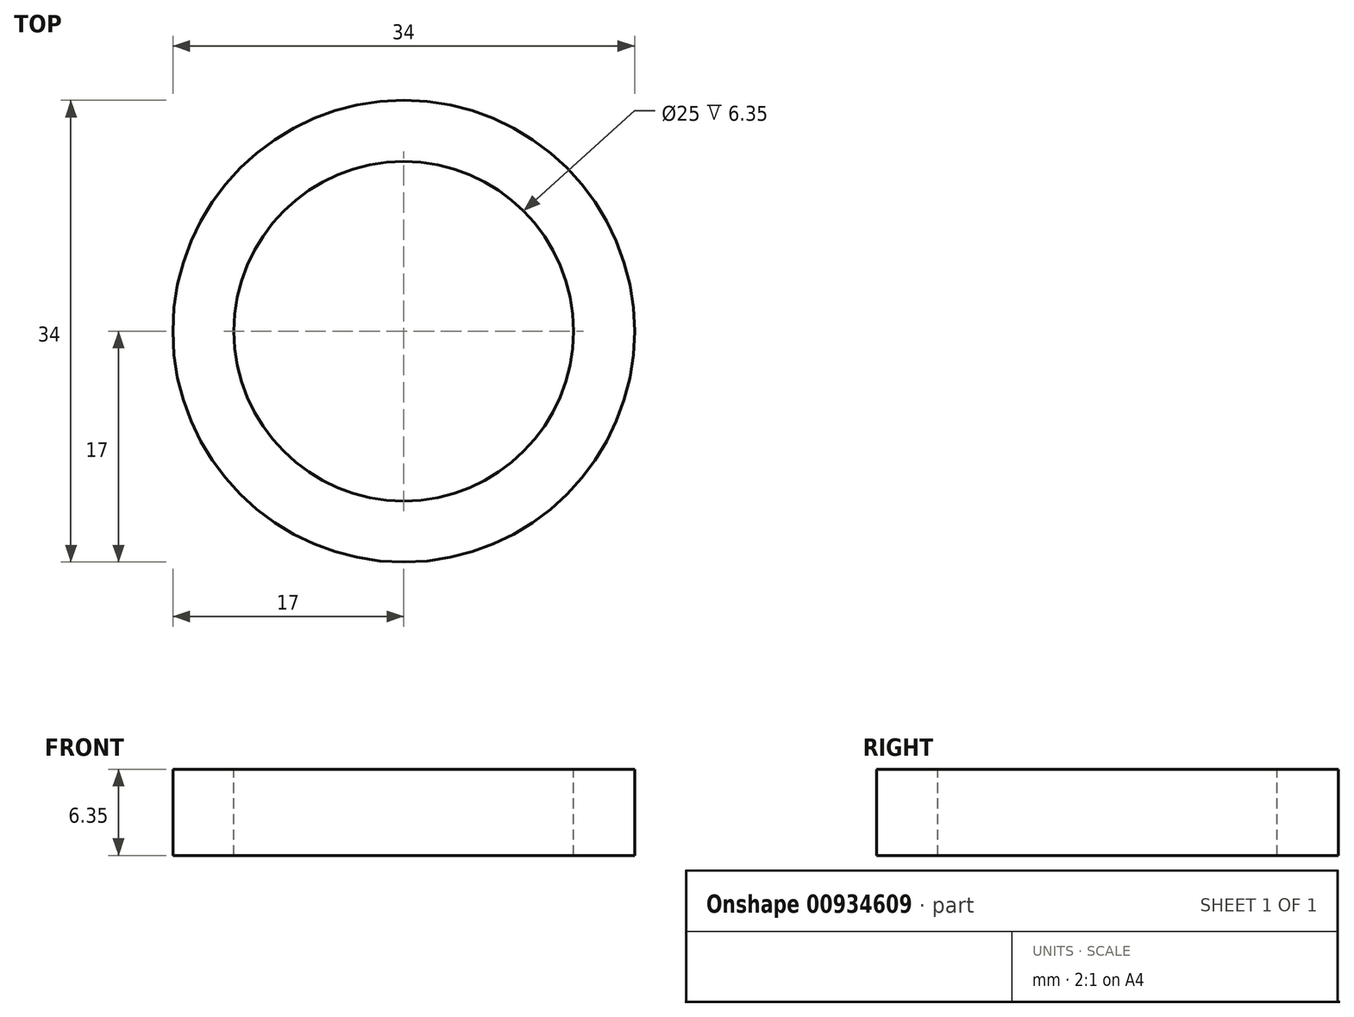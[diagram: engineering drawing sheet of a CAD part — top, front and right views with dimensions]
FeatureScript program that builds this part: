
annotation { "Feature Type Name" : "Feature", "Feature Type Description" : "" }
export const myFeature = defineFeature(function(context is Context, id is Id, definition is map)
    precondition{}
    {
        {
            var Q0;
            Q0=qCreatedBy(makeId("Top.planeOp"),FACE);
            var sketch = newSketch(context, id + "F0", { "sketchPlane" : qUnion([Q0])});
            skCircle(sketch, "E0", {"center": v(0, 0) * mm, "radius": 17 * mm});
            skSolve(sketch);
        }
        {
            var Q0;
            Q0 = qSketchRegion(id + "F0", true);
            extrude(context, id + "F1", {"entities" : qUnion([Q0]), "depth" : 6.35 * mm, "offsetDistance" : 25.4 * mm});
        }
        {
            var Q0;
            Q0=makeQuery(id+"F1.opExtrude","CAP_FACE",FACE,{"disambiguationData":[OSD([sQuery(id+"F0.wireOp",EDGE,"E0")])],"isStart":false});
            var sketch = newSketch(context, id + "F2", { "sketchPlane" : qUnion([Q0])});
            skCircle(sketch, "E1", {"center": v(0, 0) * mm, "radius": 12.5 * mm});
            skSolve(sketch);
        }
        {
            var Q0;
            Q0=makeQuery(id+"F2.imprint","IMPRINT",FACE,{"disambiguationData":[TD([[makeQuery(id+"F2.imprint","IMPRINT",EDGE,{"derivedFrom":sQuery(id+"F2.wireOp",EDGE,"E1")}),1.0]])]});
            var Q1;
            Q1=sQuery(id+"F2.wireOp",EDGE,"E1");
            extrude(context, id + "F3", {"entities" : qUnion([Q0]), "operationType" : NewBodyOperationType.REMOVE, "surfaceOperationType" : NewSurfaceOperationType.ADD, "surfaceEntities" : qUnion([Q1]), "endBound" : BoundingType.UP_TO_NEXT, "oppositeDirection" : true, "depth" : 25.4 * mm, "offsetDistance" : 25.4 * mm});
        }
    });
